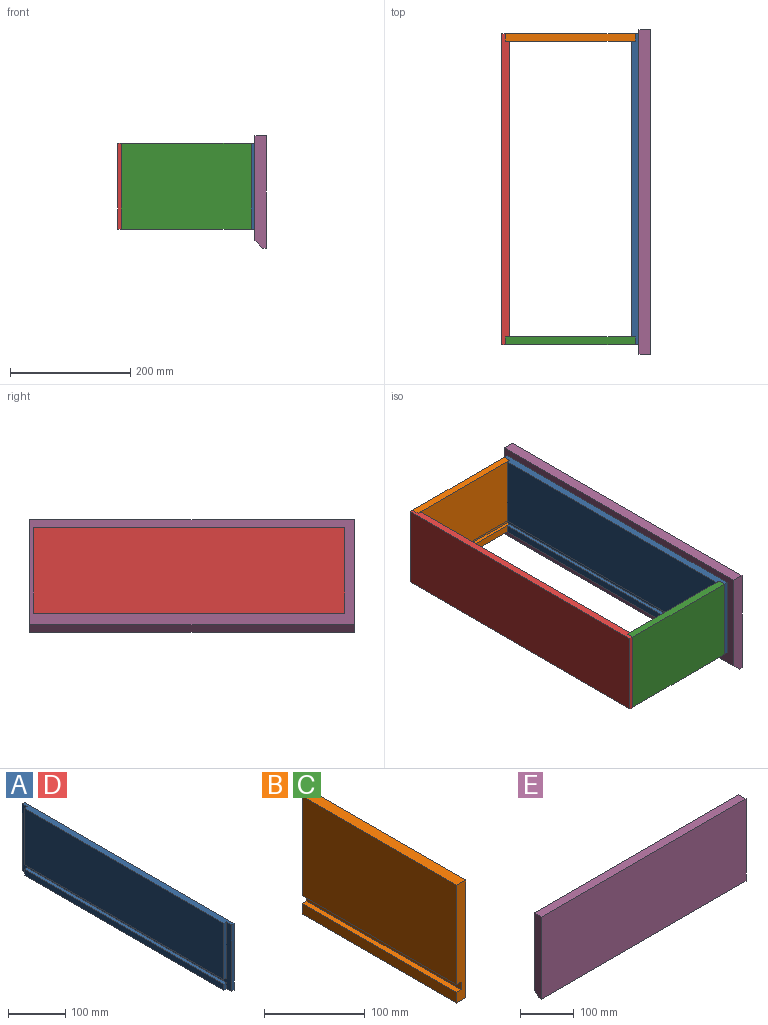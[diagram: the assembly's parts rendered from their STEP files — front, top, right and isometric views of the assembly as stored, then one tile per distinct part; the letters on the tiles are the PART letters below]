
ASSEMBLY  parts=5 mates=4
PART A: 14 faces, bbox 12.7x517.5x142.9 mm
  f0: plane 492.13x12.7mm, normal (-1,0,0), area 6250mm2, adj f6,f9,f10,f12
  f1: plane 120.65x6.35mm, normal (0,-1,0), area 766.1mm2, adj f3,f4,f11,f13
  f2: plane 120.65x6.35mm, normal (0,1,0), area 766.1mm2, adj f3,f4,f11,f13
  f3: plane 517.53x12.7mm, normal (0,0,1), area 6411.3mm2, adj f1,f2,f4,f5,f7,f8,f11
  f4: plane 492.13x120.65mm, normal (-1,0,0), area 59374.9mm2, adj f1,f2,f3,f13
  f5: plane 142.88x6.35mm, normal (0,-1,0), area 907.3mm2, adj f3,f6,f8,f11
  f6: plane 517.53x12.7mm, normal (0,0,-1), area 6411.3mm2, adj f0,f5,f7,f8,f9,f10,f11
  f7: plane 142.88x6.35mm, normal (0,1,0), area 907.3mm2, adj f3,f6,f8,f11
  f8: plane 517.53x142.88mm, normal (1,0,0), area 73941.4mm2, adj f3,f5,f6,f7
  f9: plane 12.7x6.35mm, normal (0,-1,0), area 80.6mm2, adj f0,f6,f11,f12
  f10: plane 12.7x6.35mm, normal (0,1,0), area 80.6mm2, adj f0,f6,f11,f12
  f11: plane 517.53x142.88mm, normal (-1,0,0), area 8316.5mm2, adj f1,f2,f3,f5,f6,f7,f9,f10
  f12: plane 492.13x6.35mm, normal (0,0,1), area 3125mm2, adj f0,f9,f10,f11
  f13: plane 492.13x6.35mm, normal (0,0,-1), area 3125mm2, adj f1,f2,f4,f11
PART B: 10 faces, bbox 12.7x215.9x142.9 mm
  f0: plane 215.9x12.7mm, normal (-1,0,0), area 2741.9mm2, adj f1,f2,f3,f8
  f1: plane 142.88x12.7mm, normal (0,-1,0), area 1754mm2, adj f0,f2,f4,f5,f6,f7,f8,f9
  f2: plane 215.9x12.7mm, normal (0,0,-1), area 2741.9mm2, adj f0,f1,f3,f5
  f3: plane 142.88x12.7mm, normal (0,1,0), area 1754mm2, adj f0,f2,f4,f5,f6,f7,f8,f9
  f4: plane 215.9x12.7mm, normal (0,0,1), area 2741.9mm2, adj f1,f3,f5,f6
  f5: plane 215.9x142.88mm, normal (1,0,0), area 30846.7mm2, adj f1,f2,f3,f4
  f6: plane 215.9x120.65mm, normal (-1,0,0), area 26048.3mm2, adj f1,f3,f4,f7
  f7: plane 215.9x6.35mm, normal (0,0,-1), area 1371mm2, adj f1,f3,f6,f9
  f8: plane 215.9x6.35mm, normal (0,0,1), area 1371mm2, adj f0,f1,f3,f9
  f9: plane 215.9x9.53mm, normal (-1,0,0), area 2056.4mm2, adj f1,f3,f7,f8
PART C: same geometry as B
PART D: same geometry as A
PART E: 7 faces, bbox 539.8x19.1x187.3 mm
  f0: plane 187.33x19.05mm, normal (-1,0,0), area 3487.9mm2, adj f1,f3,f4,f5,f6
  f1: plane 539.75x6.35mm, normal (0,0,-1), area 3427.4mm2, adj f0,f2,f4,f6
  f2: plane 187.33x19.05mm, normal (1,0,0), area 3487.9mm2, adj f1,f3,f4,f5,f6
  f3: plane 539.75x19.05mm, normal (0,0,1), area 10282.2mm2, adj f0,f2,f4,f5
  f4: plane 539.75x187.33mm, normal (0,-1,0), area 101108.7mm2, adj f0,f1,f2,f3
  f5: plane 539.75x174.63mm, normal (0,1,0), area 94253.8mm2, adj f0,f2,f3,f6
  f6: plane 539.75x12.7mm, normal (0,0.71,-0.71), area 9694.2mm2, adj f0,f1,f2,f5
PLACE A rot(axis=(0,0,-1),0deg) t=(-138.5,-426.32,-178.55)mm
PLACE B rot(axis=(0,0,1),90deg) t=(-132.15,78.51,-178.55)mm
PLACE C rot(axis=(0,0,-1),90deg) t=(-348.05,-413.62,-178.55)mm
PLACE D rot(axis=(0,0,-1),180deg) t=(-341.7,91.21,-178.55)mm
PLACE E rot(axis=(0,0,1),90deg) t=(-125.8,-442.19,-210.3)mm
MATE fastened C.f3 <-> A.f11  axis (1,0,0) through (-132.15,-426.32,-35.68)mm
MATE fastened B.f3 <-> D.f11  axis (-1,0,0) through (-348.05,91.21,-35.68)mm
MATE fastened B.f1 <-> A.f11  axis (1,0,0) through (-132.15,91.21,-35.68)mm
MATE fastened A.f8 <-> E.f5  axis (1,0,0) through (-125.8,-167.55,-35.68)mm
